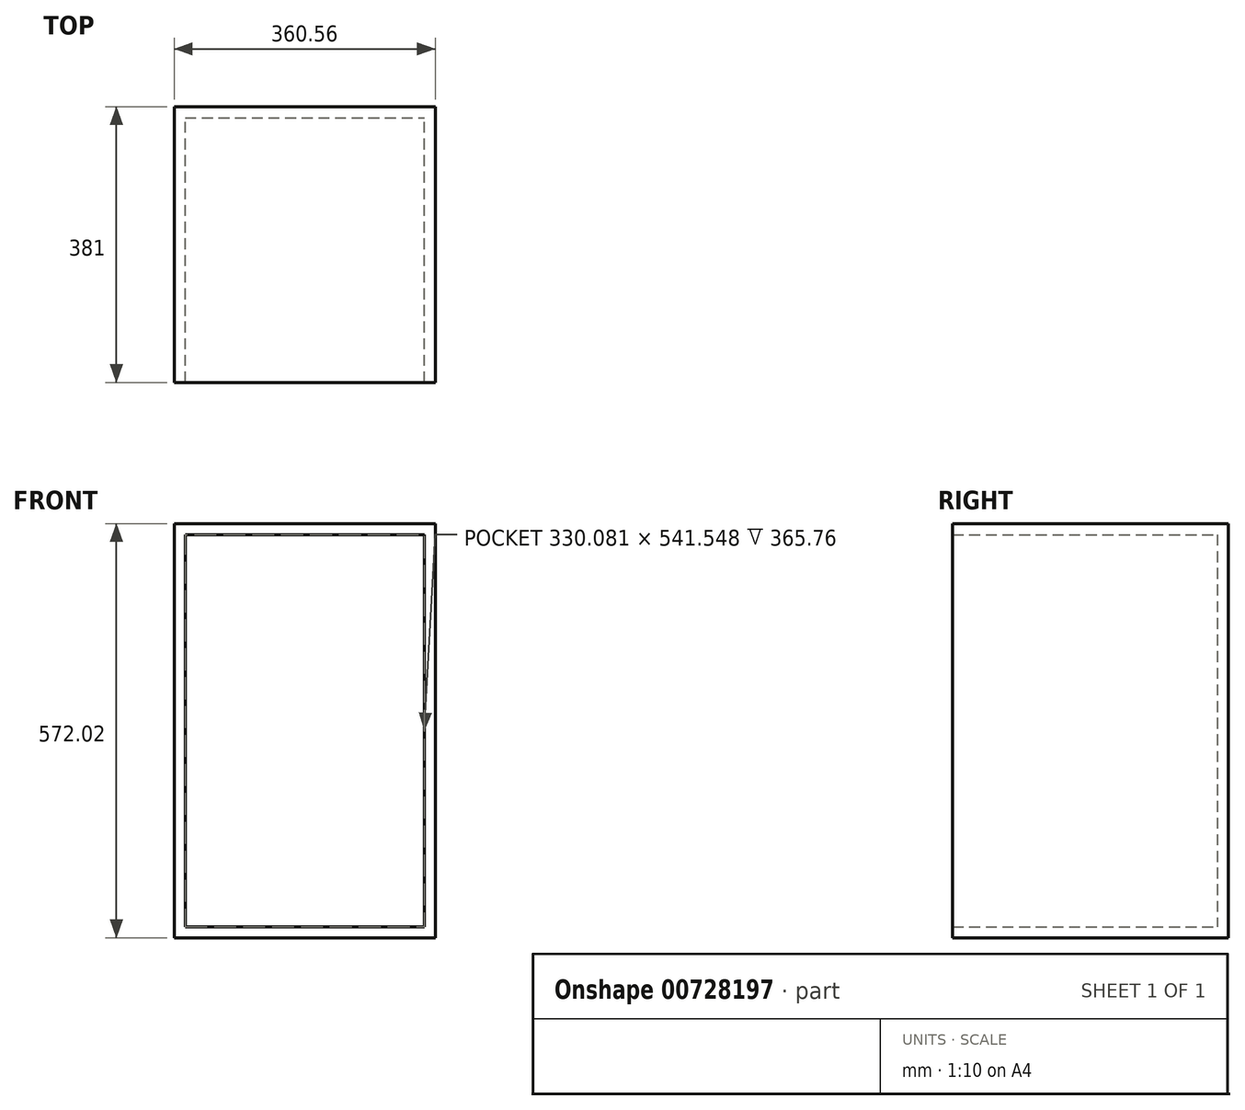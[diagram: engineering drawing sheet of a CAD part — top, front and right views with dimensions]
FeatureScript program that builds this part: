
annotation { "Feature Type Name" : "Feature", "Feature Type Description" : "" }
export const myFeature = defineFeature(function(context is Context, id is Id, definition is map)
    precondition{}
    {
        {
            var Q0;
            Q0=qCreatedBy(makeId("Front.planeOp"),FACE);
            var sketch = newSketch(context, id + "F0", { "sketchPlane" : qUnion([Q0])});
            skLineSegment(sketch, "E0.bottom", {"start": v(-40.58, 44.71) * mm, "end": v(40.58, 44.71) * mm});
            skLineSegment(sketch, "E0.top", {"start": v(-40.58, -44.71) * mm, "end": v(40.58, -44.71) * mm});
            skLineSegment(sketch, "E0.left", {"start": v(-40.58, 44.71) * mm, "end": v(-40.58, -44.71) * mm});
            skLineSegment(sketch, "E0.right", {"start": v(40.58, 44.71) * mm, "end": v(40.58, -44.71) * mm});
            skPoint(sketch, "E0.middle", {"position": v(0, 0) * mm});
            skSolve(sketch);
        }
        {
            var Q0;
            Q0=makeQuery(id+"F0.imprint","IMPRINT",FACE,{"disambiguationData":[TD([[makeQuery(id+"F0.imprint","IMPRINT",EDGE,{"derivedFrom":sQuery(id+"F0.wireOp",EDGE,"E0.bottom")}),-1.0]])]});
            extrude(context, id + "F1", {"entities" : qUnion([Q0]), "depth" : 381 * mm, "offsetDistance" : 25.4 * mm});
        }
        {
            var Q0;
            Q0=makeQuery(id+"F1.opExtrude","SWEPT_FACE",FACE,{"disambiguationData":[OSD([sQuery(id+"F0.wireOp",EDGE,"E0.bottom")])]});
            extrude(context, id + "F2", {"entities" : qUnion([Q0]), "operationType" : NewBodyOperationType.ADD, "depth" : 482.6 * mm, "offsetDistance" : 25.4 * mm});
        }
        {
            var Q0;
            {var subQ0=sQuery(id+"F0.wireOp",EDGE,"E0.right");Q0=makeQuery(id+"F2.boolean.opBoolean","MERGE",FACE,{"derivedFrom":[makeQuery(id+"F1.opExtrude","SWEPT_FACE",FACE,{"disambiguationData":[OSD([subQ0])]}),makeQuery(id+"F2.opExtrude","SWEPT_FACE",FACE,{"disambiguationData":[OSD([sQuery(id+"F0.wireOp",EDGE,"E0.bottom"),subQ0])]})]});}
            extrude(context, id + "F3", {"entities" : qUnion([Q0]), "operationType" : NewBodyOperationType.ADD, "depth" : 279.4 * mm, "offsetDistance" : 25.4 * mm});
        }
        {
            var Q0;
            {var subQ0=sQuery(id+"F0.wireOp",EDGE,"E0.right");var subQ1=sQuery(id+"F0.wireOp",EDGE,"E0.bottom");Q0=makeQuery(id+"F3.boolean.opBoolean","MERGE",FACE,{"derivedFrom":[makeQuery(id+"F2.boolean.opBoolean","MERGE",FACE,{"derivedFrom":[makeQuery(id+"F1.opExtrude","CAP_FACE",FACE,{"disambiguationData":[OSD([subQ1,sQuery(id+"F0.wireOp",EDGE,"E0.top"),sQuery(id+"F0.wireOp",EDGE,"E0.left"),subQ0])],"isStart":false}),makeQuery(id+"F2.opExtrude","SWEPT_FACE",FACE,{"disambiguationData":[OSD([subQ1]),TDD([makeQuery(id+"F1.opExtrude","CAP_EDGE",EDGE,{"disambiguationData":[OSD([subQ1])],"isStart":false})])]})]}),makeQuery(id+"F3.opExtrude","SWEPT_FACE",FACE,{"disambiguationData":[OSD([subQ1,subQ0]),TDD([makeQuery(id+"F2.boolean.opBoolean","MERGE",EDGE,{"derivedFrom":[makeQuery(id+"F1.opExtrude","CAP_EDGE",EDGE,{"disambiguationData":[OSD([subQ0])],"isStart":false}),makeQuery(id+"F2.opExtrude","SWEPT_EDGE",EDGE,{"disambiguationData":[OSD([subQ1,subQ0]),TDD([makeQuery(id+"F1.opExtrude","CAP_VERTEX",VERTEX,{"disambiguationData":[OSD([subQ1,subQ0])],"isStart":false})])]})]})])]})]});}
            shell(context, id + "F4", {"entities" : qUnion([Q0]), "thickness" : 15.24 * mm});
        }
    });
